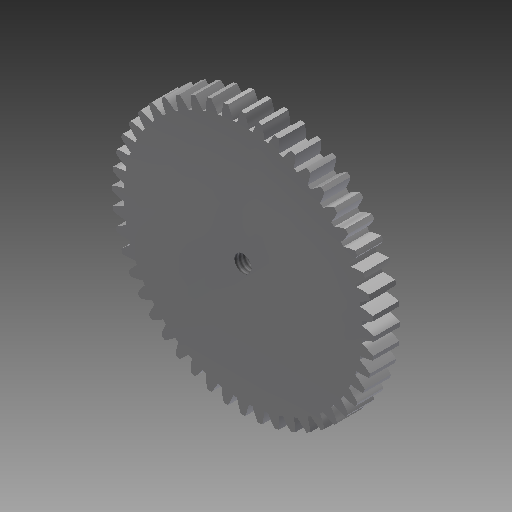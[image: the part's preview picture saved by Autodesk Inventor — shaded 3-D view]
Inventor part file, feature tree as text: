
AUTODESK INVENTOR PART (.ipt)
format: ipt  version: 2017 (Build 210142000, 142)  size: 336,384 bytes
history: native  units: mm (DEFAULTED — no unit token found)
features: plane x3, other x3, sketch x3, extrude x1, hole x1
ambient origin geometry x8: Origin, YZ Plane, XZ Plane, XY Plane, X Axis, Y Axis, Z Axis, Center Point
bodies: Solid1 (feature_tree)
feature tree (11):
  extrude  "Extrusion1"  Depth=5.0mm TaperAngle=0.0deg
  plane  "Work Plane2"
  plane  "Work Plane8"
  plane  "Work Plane9"
  other  "Spur Gear"
  hole  "Hole1"  [1 undecoded]
  sketch  "Sketch1"  dims[d0=50.0mm d1=5.0mm d2=0.0mm]
  sketch  "Sketch2"  dims[d3=48.0mm d4=10.0mm d5=0.0mm]
  other  "Srf1"
  sketch  "Sketch3"  dims[d16=43.5mm d17=0.0mm d34=0.654498mm d39=0.0mm d41=0.0mm d43=43.5mm d46=43.5mm d47=0.0mm d48=0.0mm d49=4.1656mm d50=3.302mm d51=8.331mm d52=4.0mm d53=2.0mm d54=90.0deg d55=12.3mm d56=20.594885mm]
  other  "Pitch Diameter"
note: 1 required parameter value undecoded (feature->parameter linkage not recoverable at this tier; creation-order binding heuristic only, values carry confidence <= 0.55)
